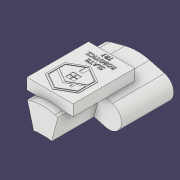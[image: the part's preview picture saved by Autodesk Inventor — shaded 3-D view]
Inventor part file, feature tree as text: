
AUTODESK INVENTOR PART (.ipt)
format: ipt  version: 2017 SP1 (Build 210196100, 196)  size: 504,832 bytes
history: native  units: in
note: dims shown in document units (in); Inventor stores cm internally (conversion verified against a paired STEP export)
features: extrude x5, sketch x5, plane x1
ambient origin geometry x8: Origin, YZ Plane, XZ Plane, XY Plane, X Axis, Y Axis, Z Axis, Center Point
bodies: Solid1 (feature_tree)
feature tree (11):
  extrude  "Extrusion1"  Depth=10.8268in TaperAngle=0.0deg
  extrude  "Extrusion2"  Depth=11.811in
  plane  "Work Plane1"
  extrude  "Extrusion3"  Depth=1.8701in
  extrude  "Extrusion4"  Depth=10.8268in
  extrude  "Extrusion5"  Depth=0.0787in TaperAngle=0.0deg
  sketch  "Sketch1"  dims[d0=6.2992in d1=3.937in d2=3.937in d3=6.2992in d4=6.2992in d5=6.2992in d6=75.0deg d7=75.0deg d8=6.2992in d9=3.937in d10=3.937in d11=0.4134in d12=0.4134in d13=4.4488in d14=8.3858in d15=0.7874in d16=12.4016in d17=0.4134in d18=0.597in d19=7.3031in d20=2.7559in d21=0.0in d22=10.8268in d23=0.0in]
  sketch  "Sketch2"  dims[d24=-6.1024in d25=11.811in]
  sketch  "Sketch3"  dims[d26=15.748in d27=1.8701in]
  sketch  "Sketch4"  dims[d28=2.8346in d29=0.0in]
  sketch  "Sketch5"  dims[d30=0.5906in d31=9.8425in d32=0.4016in d33=0.1673in d34=2.0669in d35=1.5748in d36=0.5512in d37=1.122in d38=0.5906in d39=0.9449in d40=1.8504in d41=0.9055in d42=2.0079in d43=2.0669in d44=0.9449in d45=0.9449in d46=0.9449in d47=0.9449in d48=0.9449in d49=0.9449in d50=0.9449in d51=0.9449in d54=11.811in d56=15.748in d94=0.0787in d95=0.0in d96=10.5906in d97=0.0in d98=0.7874in d99=0.7874in d100=10.8268in d101=0.0in]
